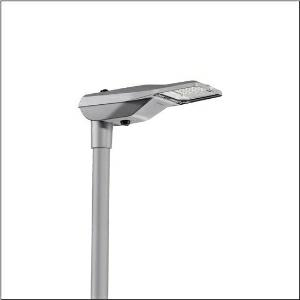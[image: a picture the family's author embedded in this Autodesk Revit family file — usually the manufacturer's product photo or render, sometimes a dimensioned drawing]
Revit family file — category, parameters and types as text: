
# Revit family: streetlight_sl_21_micro___pl52_5xe1h33t08db_704d
name_source: partatom
category: Lighting Fixtures
units: mm (PartAtom-declared; Revit-internal decimal feet)

## family parameters
Cut with Voids When Loaded = No
Host = Face
Light Source = No
Part Type = Normal
Room Calculation Point = No
Round Connector Dimension = Use Diameter
Shared = No

## types (1)
- --- (1 x LED, 5020 lm, 39.1 W, 3000K)
    Apparent Load = 39 VA
    CIE Flux Codes = 27 59 98 100 100
    Color Rendering = 70
    Color Temperature = 3000K
    Default Elevation = 1800 mm
    Description = Streetlight SL 21 micro, mast luminaire, primary light control with lens, of PMMA, primary optical cover: cover, of toughened safety glass, transparent, light distribution: PL52, light emission: direct distribution, primary light characteristic: asymmetric, installation type: side-entry, post-top, LED, High Power LED, rated luminous flux: 5.020lm, luminous efficacy: 128lm/W, light colour: 730, colour temperature: 3000K, control gear: D4i, control: flexible luminous flux parameterisation, time-dependent luminous flux control, constant luminous flux control, overheat protection, pre-setting: logarithmic dimming characteristic, mains connection: 220..240V, AC, 50/60Hz, start of lifetime: 39W, end of service life: 41W, reduction: 18W, luminaire housing, of diecast aluminium, powder-coated, Siteco® metallic grey (DB 702S), corrosivity category C5 mid according to DIN EN ISO 12944, please order mast flange separately, inclination adjustable: 0°, 5°, 10°, 15°, sealing non-destructively replaceable, multi-level sealing system, length: 528mm, width: 235mm, height: 110mm, mast flange for spigot size: 42mm (side-entry): 5XC10008XM4, 60/48mm (side-entry/post-top): 5XC10108XM2, 76/60mm (side-entry/post-top): 5XC10108XM1, Smart Interface below and above, protection rating (complete): IP66, insulation class (complete): insulation class II (safety insulation), certification: CE, ENEC, ENEC+, VDE, impact resistance: IK10, permissible operating ambient temperature for outdoor applications: -40..+50°C, standard-compliant lighting for roads and squares, packaging unit: 1 piece

Light Distribution: PL52
    Height = 110 mm
    Lamp = 1 x LED
    Lamp Light Flux = 5020 lm
    Lamp Power = 39.1 W
    Lamp count = 1
    Length = 528 mm
    Luminous efficacy = 128 lm/W
    Manufacturer = Siteco
    ModVariant = No
    Model = 5XE1H33T08DB
    Number of Poles = 1
    OnlyDefault = Yes
    Power Factor = 1
    Product Name = Streetlight SL 21 micro | PL52
    Product group = mast luminaire | pylon top
    ProductGroupID = 6100
    Protection Class = Protection class II
    Protection Degree = IP 66
    RLX_Detail_Level = 1
    RLX_Emergency_Light_Flux = 0 lm
    RLX_Emergency_Type = 0
    RLX_Emergency_Type_DB = No
    RlxData = <blob elided: 108181 chars, md5=8cecfe74>
    Socket = socket
    Standby Power = 0 W
    System Light Flux = 5020 lm
    System Power = 39 W
    Type Comments = factory setting: luminous flux: 100 % | dim-lin: 254 | 765 mA
    Type Image = l_1007239.jpg
    URL = http://relux.com
    VarID = @adj_177653
    Voltage = 0 V
    Weight = 0.00 kg
    Width = 235 mm

## geometry (parser evidence)
native form markers: Blend x4, Sweep x13
no freeform markers — native parametric forms only
